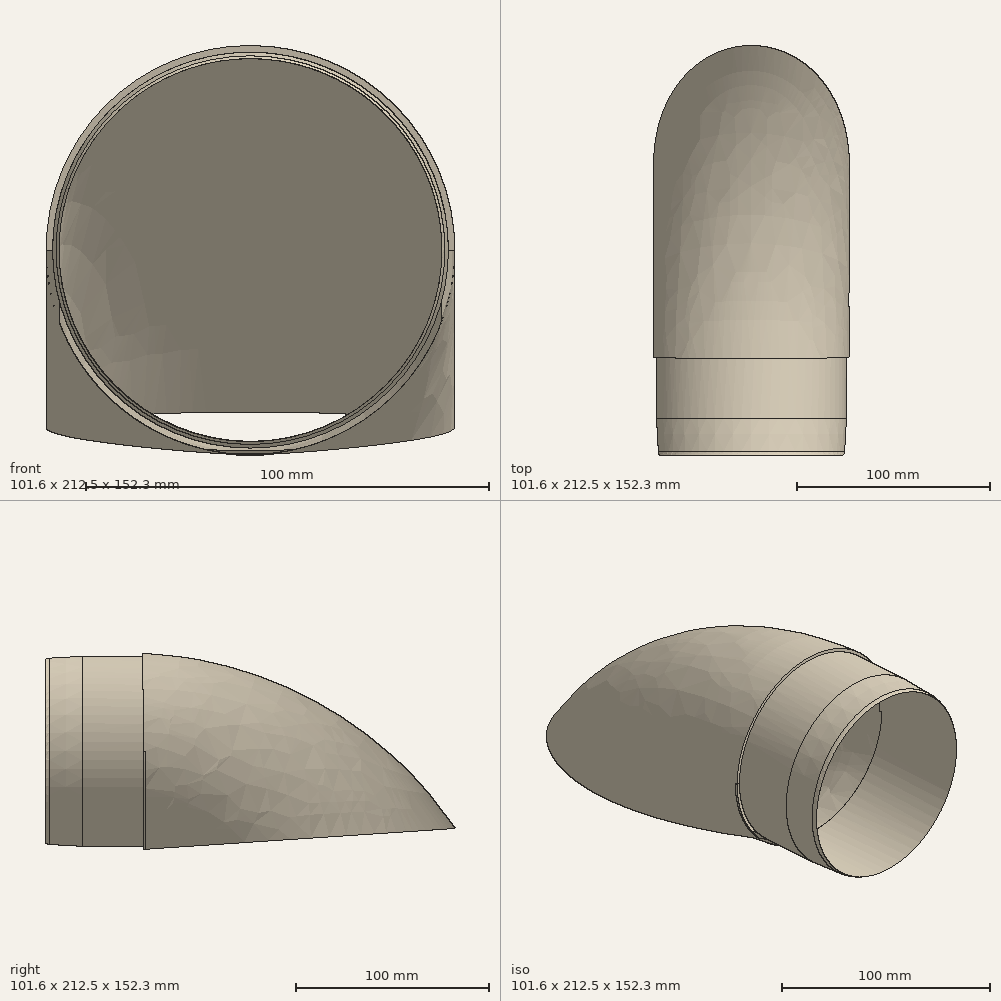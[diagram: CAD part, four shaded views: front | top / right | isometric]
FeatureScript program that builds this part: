
annotation { "Feature Type Name" : "Feature", "Feature Type Description" : "" }
export const myFeature = defineFeature(function(context is Context, id is Id, definition is map)
    precondition{}
    {
        {
            var Q0;
            Q0=qCreatedBy(makeId("Front.planeOp"),FACE);
            var sketch = newSketch(context, id + "F0", { "sketchPlane" : qUnion([Q0])});
            skCircle(sketch, "E0", {"center": v(0, 0) * mm, "radius": 50.8 * mm});
            skCircle(sketch, "E1", {"center": v(0, 0) * mm, "radius": 47.63 * mm});
            skSolve(sketch);
        }
        {
            var Q0;
            Q0=qSketchRegion(id+"F0",true);
            extrude(context, id + "F1", {"entities" : qUnion([Q0]), "oppositeDirection" : true, "depth" : 1.27 * mm, "hasSecondDirection" : true, "secondDirectionOppositeDirection" : false, "secondDirectionDepth" : 50.8 * mm});
        }
        {
            var Q0;
            Q0=qCreatedBy(makeId("Front.planeOp"),FACE);
            var sketch = newSketch(context, id + "F2", { "sketchPlane" : qUnion([Q0])});
            skCircle(sketch, "E2", {"center": v(0, 0) * mm, "radius": 49.21 * mm});
            skCircle(sketch, "E3", {"center": v(0, 0) * mm, "radius": 50.8 * mm});
            skSolve(sketch);
        }
        {
            var Q0;
            Q0=qSketchRegion(id+"F2",true);
            extrude(context, id + "F3", {"entities" : qUnion([Q0]), "operationType" : NewBodyOperationType.REMOVE, "endBound" : BoundingType.THROUGH_ALL, "depth" : 25.4 * mm});
        }
        {
            var Q0;
            Q0=makeQuery(id+"F3.boolean.opBoolean","INTERSECT",EDGE,{"derivedFrom":[makeQuery(id+"F1.opExtrude","CAP_FACE",FACE,{"disambiguationData":[OSD([sQuery(id+"F0.wireOp",EDGE,"E0"),sQuery(id+"F0.wireOp",EDGE,"E1")])],"isStart":true}),makeQuery(id+"F3.opExtrude","SWEPT_FACE",FACE,{"disambiguationData":[OSD([sQuery(id+"F2.wireOp",EDGE,"E2")])]})]});
            chamfer(context, id + "F4", {"entities" : qUnion([Q0]), "chamferType" : ChamferType.TWO_OFFSETS, "width1" : 19.05 * mm, "oppositeDirection" : false, "width2" : 1.02 * mm, "tangentPropagation" : true});
        }
        {
            var Q0;
            {var subQ0=makeQuery(id+"F1.opExtrude","CAP_FACE",FACE,{"disambiguationData":[OSD([sQuery(id+"F0.wireOp",EDGE,"E0"),sQuery(id+"F0.wireOp",EDGE,"E1")])],"isStart":true});Q0=makeQuery(id+"F4.opChamfer","BLEND_EDGE",EDGE,{"blendedFrom":[makeQuery(id+"F3.boolean.opBoolean","INTERSECT",EDGE,{"derivedFrom":[subQ0,makeQuery(id+"F3.opExtrude","SWEPT_FACE",FACE,{"disambiguationData":[OSD([sQuery(id+"F2.wireOp",EDGE,"E2")])]})]}),subQ0],"blendedInto":[subQ0]});}
            fillet(context, id + "F5", {"entities" : qUnion([Q0]), "radius" : 5.08 * mm, "tangentPropagation" : true, "allowEdgeOverflow" : false});
        }
        {
            var Q0;
            Q0=qCreatedBy(makeId("Right.planeOp"),FACE);
            var sketch = newSketch(context, id + "F6", { "sketchPlane" : qUnion([Q0])});
            skArc(sketch, "E4", {"start": v(146.53, -156.84) * mm, "mid": v(104.4, -49.33) * mm, "end": v(0, 0) * mm});
            skLineSegment(sketch, "E5", {"start": v(146.53, -156.84) * mm, "end": v(0, 0) * mm});
            skSolve(sketch);
        }
        {
            var Q0;
            Q0=makeQuery(id+"F1.opExtrude","CAP_FACE",FACE,{"disambiguationData":[OSD([sQuery(id+"F0.wireOp",EDGE,"E0"),sQuery(id+"F0.wireOp",EDGE,"E1")])],"isStart":false});
            var Q1;
            Q1=sQuery(id+"F6.wireOp",EDGE,"E4");
            sweep(context, id + "F7", {"operationType" : NewBodyOperationType.ADD, "profiles" : qUnion([Q0]), "path" : qUnion([Q1])});
        }
        {
            var Q0;
            Q0=makeQuery(id+"F7.opSweep","CAP_FACE",FACE,{"disambiguationData":[OSD([sQuery(id+"F0.wireOp",EDGE,"E0"),sQuery(id+"F0.wireOp",EDGE,"E1"),sQuery(id+"F6.wireOp",VERTEX,"E4.start")])],"isStart":false});
            var sketch = newSketch(context, id + "F8", { "sketchPlane" : qUnion([Q0])});
            skLineSegment(sketch, "E6.bottom", {"start": v(-52.04, 0) * mm, "end": v(52.02, 0) * mm});
            skLineSegment(sketch, "E6.top", {"start": v(-52.04, -193.04) * mm, "end": v(52.02, -193.04) * mm});
            skLineSegment(sketch, "E6.left", {"start": v(-52.04, 0) * mm, "end": v(-52.04, -193.04) * mm});
            skLineSegment(sketch, "E6.right", {"start": v(52.02, 0) * mm, "end": v(52.02, -193.04) * mm});
            skSolve(sketch);
        }
        {
            var Q0;
            Q0=qSketchRegion(id+"F8",true);
            var Q1;
            Q1=makeQuery(id+"F1.opExtrude","SWEPT_BODY",BODY,{"disambiguationData":[OSD([sQuery(id+"F0.wireOp",EDGE,"E0"),sQuery(id+"F0.wireOp",EDGE,"E1")])]});
            extrude(context, id + "F9", {"entities" : qUnion([Q0]), "operationType" : NewBodyOperationType.REMOVE, "oppositeDirection" : true, "endBoundEntityBody" : qUnion([Q1]), "depth" : 115.57 * mm});
        }
    });
